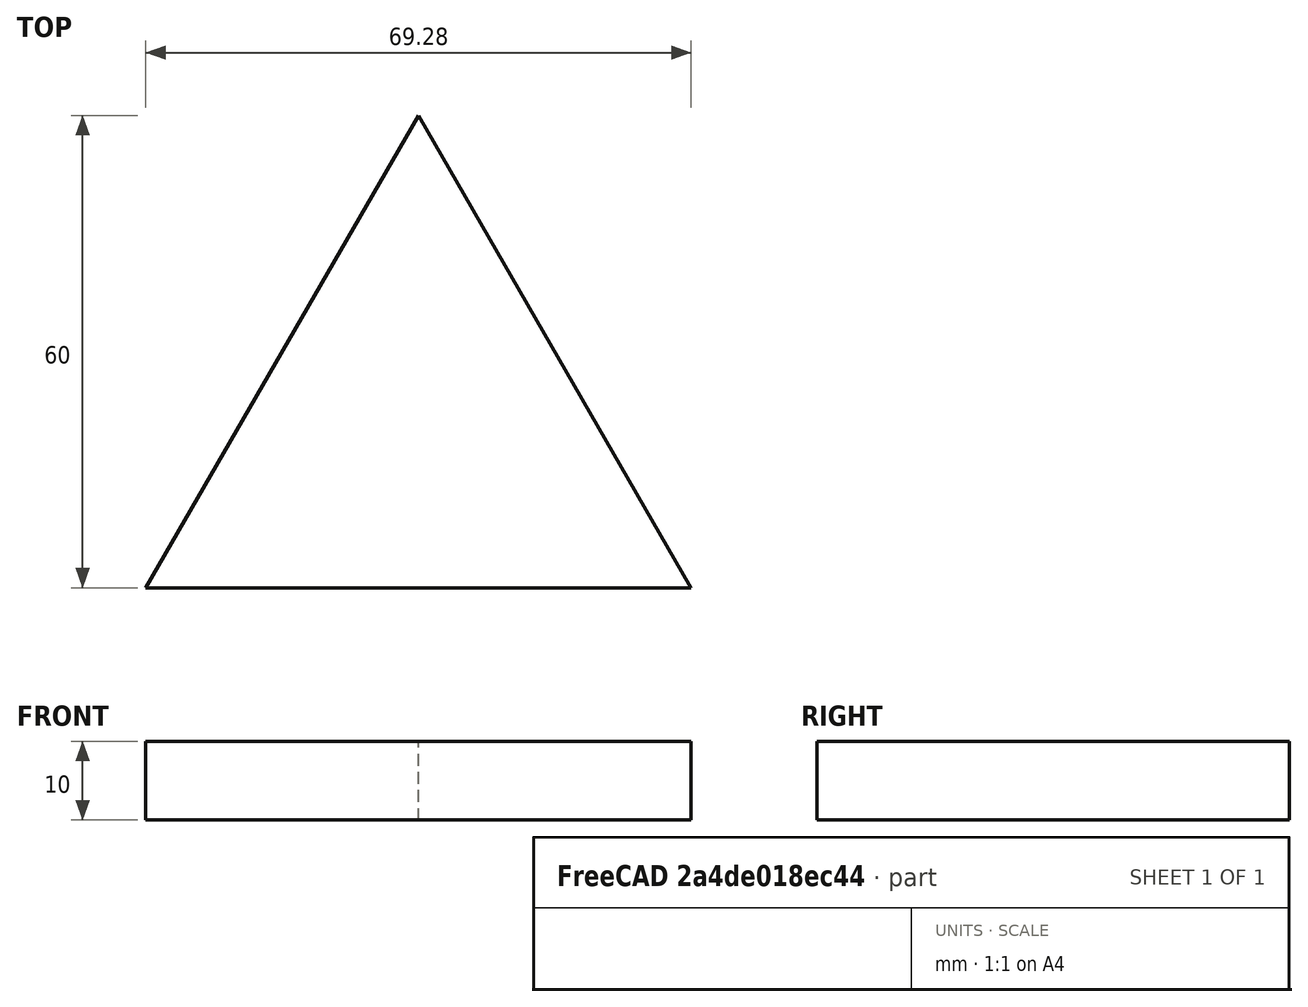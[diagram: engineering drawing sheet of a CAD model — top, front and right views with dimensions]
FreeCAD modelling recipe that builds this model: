
FCSTD DOCUMENT  (FreeCAD 0.21R33694 (Git))
Label: OJT1_T020_P01_triangle_perfecte
License: All rights reserved
LicenseURL: http://en.wikipedia.org/wiki/All_rights_reserved
objects: Sketcher::SketchObject×1, PartDesign::Pad×1, PartDesign::Body×1
note: 4 computed .brp shape members not serialized (recipe doc carries the construction recipe); baked Part::Feature solids carry a one-line shape summary decoded from their .brp

FEATURE [Sketcher::SketchObject] Sketch
  FullyConstrained = false
  MapMode = 5
  Support = -> [XY_Plane]
  sketch-geometry (4):
    g0: LineSegment StartX=0 StartY=33.8198 StartZ=0 EndX=34.641 EndY=-26.1802 EndZ=0
    g1: LineSegment StartX=34.641 StartY=-26.1802 StartZ=0 EndX=-34.641 EndY=-26.1802 EndZ=0
    g2: LineSegment StartX=-34.641 StartY=-26.1802 StartZ=0 EndX=0 EndY=33.8198 EndZ=0
    g3: LineSegment StartX=0 StartY=33.8198 StartZ=0 EndX=0 EndY=-26.1802 EndZ=0
  constraints (10):
    c: Coincident(g0,g1)
    c: Coincident(g1,g2)
    c: Coincident(g2,g0)
    c: Horizontal(g1)
    c: Vertical(g3)
    c: Coincident(g3,g0)
    c: Symmetric(g0,g1,g3)
    c: PointOnObject(g0,g-2)
    c: Angle(g1,g2) = 1.0472
    c: DistanceY(g3,g3) = 60
FEATURE [PartDesign::Pad] Pad
  Direction = (0,0,1)
  Length = 10
  Length2 = 10
  Profile = -> Sketch
  ReferenceAxis = -> Sketch [N_Axis]
  Type = 0
FEATURE [PartDesign::Body] Body
  Group = -> [Sketch,Pad]
  Origin = -> Origin
  Tip = -> Pad
